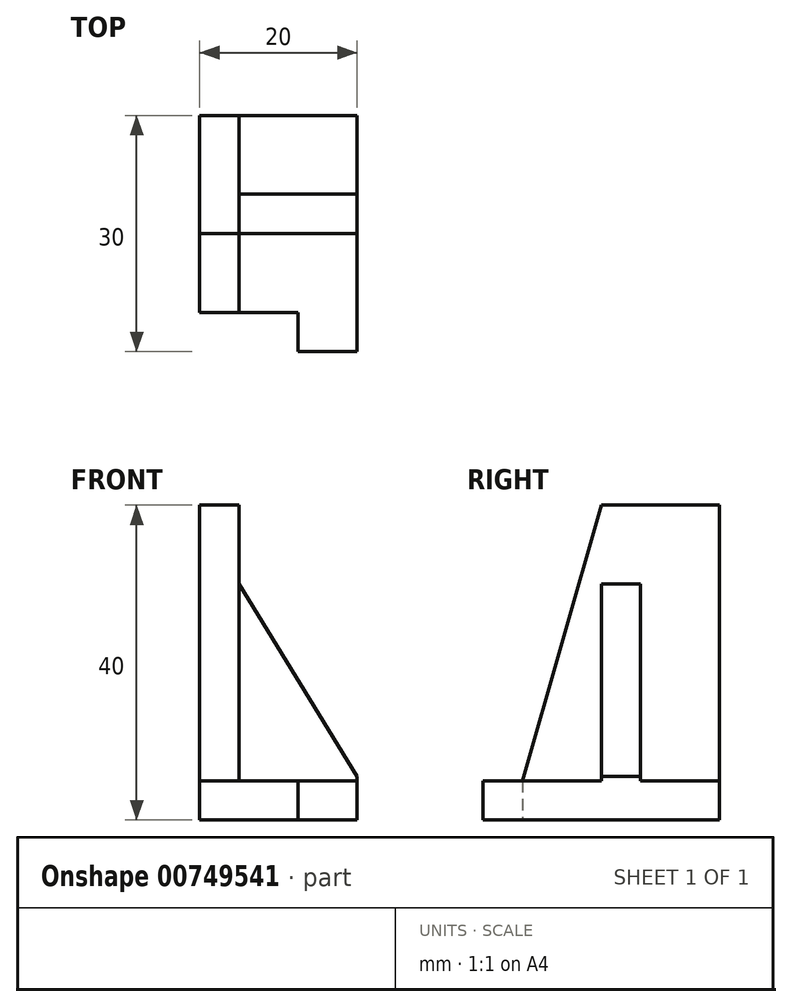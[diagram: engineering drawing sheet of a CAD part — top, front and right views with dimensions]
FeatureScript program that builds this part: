
annotation { "Feature Type Name" : "Feature", "Feature Type Description" : "" }
export const myFeature = defineFeature(function(context is Context, id is Id, definition is map)
    precondition{}
    {
        {
            var Q0;
            Q0=qCreatedBy(makeId("Top.planeOp"),FACE);
            var sketch = newSketch(context, id + "F0", { "sketchPlane" : qUnion([Q0])});
            skLineSegment(sketch, "E0", {"start": v(0, 0) * mm, "end": v(12.5, 0) * mm});
            skLineSegment(sketch, "E1", {"start": v(12.5, 0) * mm, "end": v(12.5, -5) * mm});
            skLineSegment(sketch, "E2", {"start": v(12.5, -5) * mm, "end": v(20, -5) * mm});
            skLineSegment(sketch, "E3", {"start": v(20, -5) * mm, "end": v(20, 25) * mm});
            skLineSegment(sketch, "E4", {"start": v(20, 25) * mm, "end": v(0, 25) * mm});
            skLineSegment(sketch, "E5", {"start": v(0, 25) * mm, "end": v(0, 0) * mm});
            skSolve(sketch);
        }
        {
            var Q0;
            Q0=makeQuery(id+"F0.imprint","IMPRINT",FACE,{"disambiguationData":[TD([[makeQuery(id+"F0.imprint","IMPRINT",EDGE,{"derivedFrom":sQuery(id+"F0.wireOp",EDGE,"E0")}),1.0]])]});
            extrude(context, id + "F1", {"entities" : qUnion([Q0]), "depth" : 5 * mm, "offsetDistance" : 25 * mm});
        }
        {
            var Q0;
            Q0=qCreatedBy(makeId("Right.planeOp"),FACE);
            var sketch = newSketch(context, id + "F2", { "sketchPlane" : qUnion([Q0])});
            skLineSegment(sketch, "E6", {"start": v(0, 5) * mm, "end": v(25, 5) * mm});
            skLineSegment(sketch, "E7", {"start": v(25, 5) * mm, "end": v(25, 40) * mm});
            skLineSegment(sketch, "E8", {"start": v(25, 40) * mm, "end": v(10, 40) * mm});
            skLineSegment(sketch, "E9", {"start": v(10, 40) * mm, "end": v(0, 5) * mm});
            skSolve(sketch);
        }
        {
            var Q0;
            Q0=makeQuery(id+"F2.imprint","IMPRINT",FACE,{"disambiguationData":[TD([[makeQuery(id+"F2.imprint","IMPRINT",EDGE,{"derivedFrom":sQuery(id+"F2.wireOp",EDGE,"E6")}),1.0]])]});
            extrude(context, id + "F3", {"entities" : qUnion([Q0]), "operationType" : NewBodyOperationType.ADD, "depth" : 5 * mm, "offsetDistance" : 25 * mm});
        }
        {
            var Q0;
            Q0=qCreatedBy(makeId("Right.planeOp"),FACE);
            var sketch = newSketch(context, id + "F4", { "sketchPlane" : qUnion([Q0])});
            skLineSegment(sketch, "E10", {"start": v(15, 5) * mm, "end": v(10, 5) * mm});
            skLineSegment(sketch, "E11", {"start": v(10, 5) * mm, "end": v(10, 30) * mm});
            skLineSegment(sketch, "E12", {"start": v(10, 30) * mm, "end": v(15, 30) * mm});
            skLineSegment(sketch, "E13", {"start": v(15, 30) * mm, "end": v(15, 5) * mm});
            skSolve(sketch);
        }
        {
            var Q0;
            Q0=makeQuery(id+"F4.imprint","IMPRINT",FACE,{"disambiguationData":[TD([[makeQuery(id+"F4.imprint","IMPRINT",EDGE,{"derivedFrom":sQuery(id+"F4.wireOp",EDGE,"E10")}),-1.0]])]});
            extrude(context, id + "F5", {"entities" : qUnion([Q0]), "operationType" : NewBodyOperationType.ADD, "depth" : 20 * mm, "offsetDistance" : 25 * mm});
        }
        {
            var Q0;
            Q0=qCreatedBy(makeId("Front.planeOp"),FACE);
            var sketch = newSketch(context, id + "F6", { "sketchPlane" : qUnion([Q0])});
            skLineSegment(sketch, "E14", {"start": v(5, 30) * mm, "end": v(20.34, 5) * mm});
            skLineSegment(sketch, "E15", {"start": v(20.34, 5) * mm, "end": v(20.34, 30) * mm});
            skLineSegment(sketch, "E16", {"start": v(20.34, 30) * mm, "end": v(5, 30) * mm});
            skSolve(sketch);
        }
        {
            var Q0;
            Q0=makeQuery(id+"F6.imprint","IMPRINT",FACE,{"disambiguationData":[TD([[makeQuery(id+"F6.imprint","IMPRINT",EDGE,{"derivedFrom":sQuery(id+"F6.wireOp",EDGE,"E14")}),1.0]])]});
            extrude(context, id + "F7", {"entities" : qUnion([Q0]), "operationType" : NewBodyOperationType.REMOVE, "oppositeDirection" : true, "depth" : 25 * mm, "offsetDistance" : 25 * mm});
        }
    });
